# Revit family: Hager-VEGA-Surface_mounted-IP40-With_Cover-With_DIN-Hosted-CH-it
name_source: partatom
category: Electrical Equipment
units: mm (PartAtom-declared; Revit-internal decimal feet)

## family parameters
Cut with Voids When Loaded = No
Host = Face
Maintain Annotation Orientation = Yes
Panel Configuration = Two Columns, Circuits Across
Part Type = Panelboard
Room Calculation Point = No
Round Connector Dimension = Use Diameter
Shared = No

## types (7) — shared parameters
BC_MODEL_ID = 1546989
BC_OBJECT_ID = 513428
BC_OBJECT_VERSION = #9
Code hager = ADD-EC000214_EU
EF000003 - modo di montaggio = apparente
EF000008 - larghezza = 400 mm  [stored 1.31234 ft]
EF000024 - resistente ai raggi UV = No
EF000049 - profondità = 146 mm  [stored 0.479003 ft]
EF000116 - numero RAL = 9010
EF000118 - con piastra di montaggio = No
EF001062 - versione EMC = No
EF001134 - barra DIN = Yes
EF002950 - numero di unità modulari = 18
EF005474 - grado di protezione (IP) = IP40
EF006244 - coperchio/porta trasparente = No
EF006306 - con serratura = No
EF015777 - morsettiera a conduttore neutro = No
ETIM class code = EC000214
ETIM class name = Small distribution board
HG000001 - Numero di colonne = 1
HG000002-with door or cover-it = Yes
HG000003-Range-it = VEGA
HG000005-Thickness-it = 2 mm  [stored 0.00656168 ft]
HG000006-Flush mounted-it = No
HG000009-Double swing door-it = No
HG000010-Asymmetric doors-it = No
HG000011-Empty rows from bottom-it = No
HG000012-Door swing angle-it = 90.00°
HG000013-Door on the left-it = No
HG000014-Door on the right-it = Yes
HG000015-Clearance visibility-it = Yes
HG000016-Door 3D visibility-it = Yes
HG000017-Distance between poles-it = 18 mm  [stored 0.0590551 ft]
HG000060-RAL-number = 9010
HG000099-Onfly Template ID-it-CH = 507532
HGEF0002950-larghezza in unità di suddivisione = 18
Manufacturer = Hager
Name = VEGA-Surface_mounted-IP40-With_Cover-With_DIN-CH
Name BIM&CO = Electricity
Name hager = ADD_Enclosures_EC000214
Uniformat = Low Tension Service & Dist.
Uniformat code = D501001
zero-valued in all types: Default Elevation, EF000218 - profondità di montaggio, EF000332 - altezza di installazione, EF000846 - larghezza di montaggio, EF001131 - profondità interna, HG000007-Number of empty columns-it, HG000008-Number of empty rows-it

## per-type parameters (varying)
| type | BC_VARIANT_ID | EF000007 - colore | EF000040 - altezza | EF000266 - numero di file | EF001088 - possibilità di applicazione | EF004462 - tipo di chiusura | EF009212 - tipo di coperchio | EF015776 - morsetto di messa a terra | EF015941 - porta di trasmissione del segnale | HG000004-Manufacturer reference-it | HGEF000266-Numero di file |
| VEGA-Surface_mounted_W400_H325_D146_18_Modular_Spacing-VB118B | 1173735 | bianco | 325 mm  [stored 1.06627 ft] | 1 | Yes | altri | chiuso | Yes | Yes | VB118B | 1 |
| VEGA-Surface_mounted_W400_H475_D146_18_Modular_Spacing-VB218B | 1173736 | bianco | 475 mm  [stored 1.5584 ft] | 2 | Yes | altri | chiuso | Yes | Yes | VB218B | 2 |
| VEGA-Surface_mounted_W400_H475_D146_18_Modular_Spacing-VB218R | 1173738 |  | 475 mm  [stored 1.5584 ft] | 2 | No |  |  | No | No | VB218R | 2 |
| VEGA-Surface_mounted_W400_H625_D146_18_Modular_Spacing-VB318B | 1173739 | bianco | 625 mm  [stored 2.05052 ft] | 3 | Yes | altri | chiuso | Yes | Yes | VB318B | 3 |
| VEGA-Surface_mounted_W400_H625_D146_18_Modular_Spacing-VB318R | 1173740 |  | 625 mm  [stored 2.05052 ft] | 3 | No |  |  | No | No | VB318R | 3 |
| VEGA-Surface_mounted_W400_H775_D146_18_Modular_Spacing-VB418B | 1173741 | bianco | 775 mm  [stored 2.54265 ft] | 4 | Yes | altri | chiuso | Yes | Yes | VB418B | 4 |
| VEGA-Surface_mounted_W400_H775_D146_18_Modular_Spacing-VB418R | 1173742 |  | 775 mm  [stored 2.54265 ft] | 4 | No |  |  | No | No | VB418R | 4 |

note: column(s) folded — value = type name in every type: Reference

note: [stored X ft] marks values corroborated as IEEE doubles in the binary element streams (Revit-internal decimal feet)

## geometry (parser evidence)
native form markers: Sweep x14
no freeform markers — native parametric forms only
